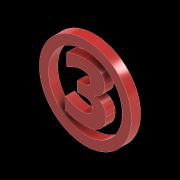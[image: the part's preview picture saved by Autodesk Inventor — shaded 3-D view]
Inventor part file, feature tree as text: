
AUTODESK INVENTOR PART (.ipt)
format: ipt  version: 2020 (Build 240168000, 168)  size: 184,320 bytes
history: native  units: mm
features: other x5, extrude x2, sketch x2
ambient origin geometry x8: Origin, YZ Plane, XZ Plane, XY Plane, X Axis, Y Axis, Z Axis, Center Point
bodies: Body1 (feature_tree)
feature tree (9):
  other  "自動販賣機.ipt"
  extrude  "擠出1"  Depth=10.0mm
  extrude  "擠出2"  Depth=10.0mm TaperAngle=0.0deg
  other  "實體49::自動販賣機.ipt"
  other  "標籤特徵1"
  sketch  "草圖1"
  sketch  "草圖2"
  other  "實體1"
  other  "投影切割邊1"
